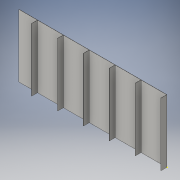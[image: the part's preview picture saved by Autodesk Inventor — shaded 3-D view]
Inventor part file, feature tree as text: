
AUTODESK INVENTOR PART (.ipt)
format: ipt  version: 2016 (Build 200138000, 138)  size: 153,088 bytes
history: native  units: in
note: dims shown in document units (in); Inventor stores cm internally (conversion verified against a paired STEP export)
features: sketch x8, extrude x7
ambient origin geometry x8: Origin, YZ Plane, XZ Plane, XY Plane, X Axis, Y Axis, Z Axis, Center Point
bodies: Solid1 (feature_tree)
feature tree (15):
  extrude  "Extrusion1"  Depth=3.4in
  extrude  "Extrusion2"  Depth=0.01in
  sketch  "Sketch3"  dims[d5=0.315in d6=0.0in d7=0.01in]
  extrude  "Extrusion3"  Depth=0.01in
  extrude  "Extrusion4"  Depth=0.01in
  extrude  "Extrusion5"  Depth=0.01in
  extrude  "Extrusion6"  Depth=0.315in TaperAngle=0.0deg
  extrude  "Extrusion7"  Depth=0.315in TaperAngle=0.0deg
  sketch  "Sketch1"  dims[d0=8.0in d1=3.4in]
  sketch  "Sketch2"  dims[d2=0.01in d3=0.0in d4=0.01in]
  sketch  "Sketch4"  dims[d8=0.315in d9=0.0in d10=0.01in]
  sketch  "Sketch5"  dims[d11=0.01in d12=0.01in]
  sketch  "Sketch6"  dims[d13=0.01in d14=0.315in d15=0.0in]
  sketch  "Sketch7"  dims[d16=0.01in d17=0.315in d18=0.0in]
  sketch  "Sketch8"  dims[d19=0.01in d20=0.315in d21=0.0in d22=0.01in d23=0.315in d24=0.0in]
